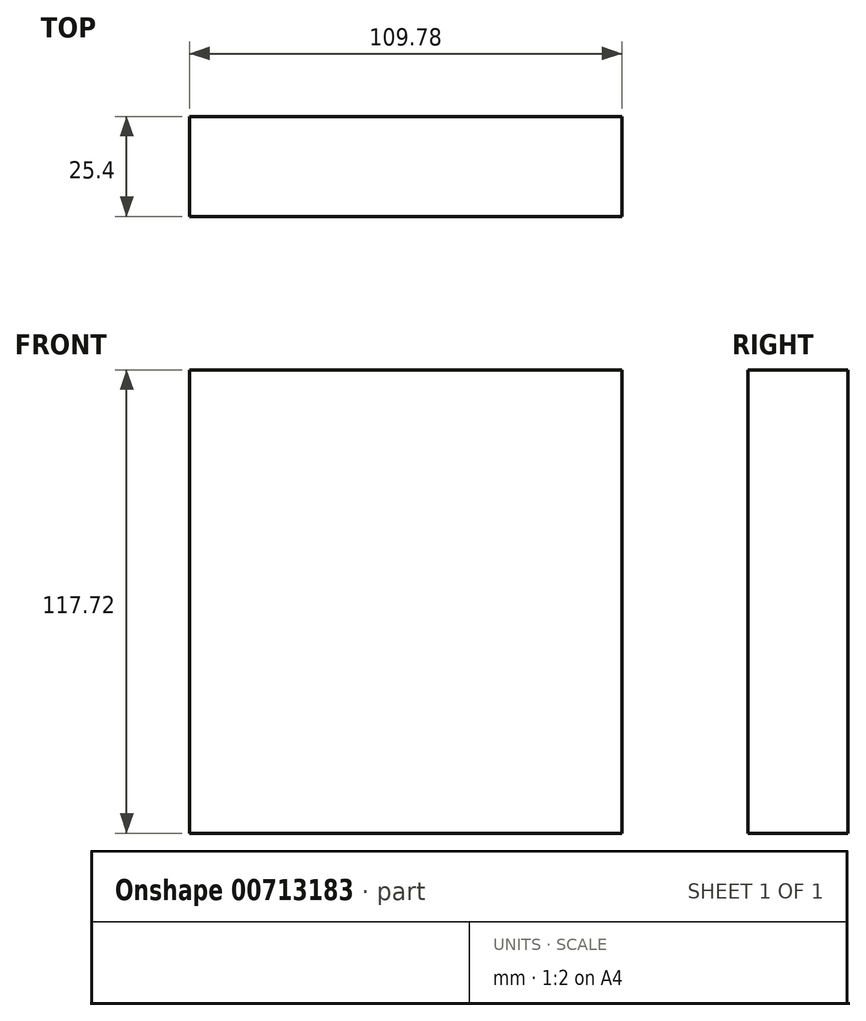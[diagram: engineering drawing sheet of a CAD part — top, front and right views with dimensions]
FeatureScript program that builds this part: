
annotation { "Feature Type Name" : "Feature", "Feature Type Description" : "" }
export const myFeature = defineFeature(function(context is Context, id is Id, definition is map)
    precondition{}
    {
        {
            var Q0;
            Q0=qCreatedBy(makeId("Front.planeOp"),FACE);
            var sketch = newSketch(context, id + "F0", { "sketchPlane" : qUnion([Q0])});
            skLineSegment(sketch, "E0.bottom", {"start": v(54.89, 58.86) * mm, "end": v(-54.89, 58.86) * mm});
            skLineSegment(sketch, "E0.top", {"start": v(54.89, -58.86) * mm, "end": v(-54.89, -58.86) * mm});
            skLineSegment(sketch, "E0.left", {"start": v(54.89, 58.86) * mm, "end": v(54.89, -58.86) * mm});
            skLineSegment(sketch, "E0.right", {"start": v(-54.89, 58.86) * mm, "end": v(-54.89, -58.86) * mm});
            skPoint(sketch, "E0.middle", {"position": v(0, 0) * mm});
            skSolve(sketch);
        }
        {
            var Q0;
            Q0 = qSketchRegion(id + "F0", true);
            extrude(context, id + "F1", {"entities" : qUnion([Q0]), "depth" : 25.4 * mm, "offsetDistance" : 25.4 * mm});
        }
    });
